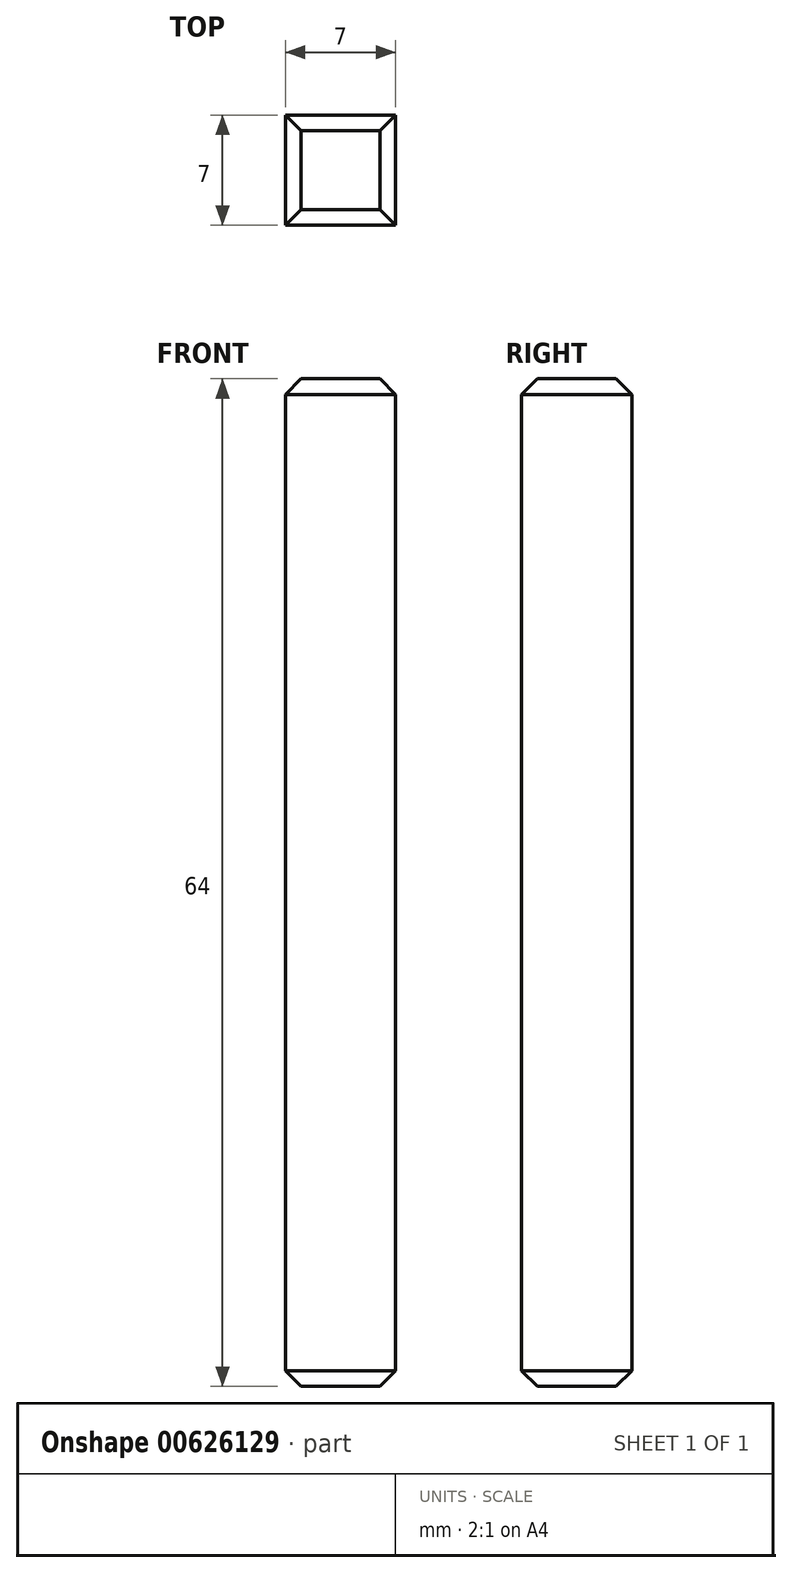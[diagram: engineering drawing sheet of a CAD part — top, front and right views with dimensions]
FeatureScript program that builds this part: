
annotation { "Feature Type Name" : "Feature", "Feature Type Description" : "" }
export const myFeature = defineFeature(function(context is Context, id is Id, definition is map)
    precondition{}
    {
        {
            var Q0;
            Q0=qCreatedBy(makeId("Front.planeOp"),FACE);
            var sketch = newSketch(context, id + "F0", { "sketchPlane" : qUnion([Q0])});
            skLineSegment(sketch, "E0.bottom", {"start": v(-3.5, 32) * mm, "end": v(3.5, 32) * mm});
            skLineSegment(sketch, "E0.top", {"start": v(-3.5, -32) * mm, "end": v(3.5, -32) * mm});
            skLineSegment(sketch, "E0.left", {"start": v(-3.5, 32) * mm, "end": v(-3.5, -32) * mm});
            skLineSegment(sketch, "E0.right", {"start": v(3.5, 32) * mm, "end": v(3.5, -32) * mm});
            skPoint(sketch, "E0.middle", {"position": v(0, 0) * mm});
            skSolve(sketch);
        }
        {
            var Q0;
            Q0=makeQuery(id+"F0.imprint","IMPRINT",FACE,{"disambiguationData":[TD([[makeQuery(id+"F0.imprint","IMPRINT",EDGE,{"derivedFrom":sQuery(id+"F0.wireOp",EDGE,"E0.bottom")}),-1.0]])]});
            extrude(context, id + "F1", {"entities" : qUnion([Q0]), "depth" : 7 * mm, "offsetDistance" : 25 * mm});
        }
        {
            var Q0;
            Q0=makeQuery(id+"F1.opExtrude","CAP_EDGE",EDGE,{"disambiguationData":[OSD([sQuery(id+"F0.wireOp",EDGE,"E0.bottom")])],"isStart":false});
            var Q1;
            Q1=makeQuery(id+"F1.opExtrude","SWEPT_EDGE",EDGE,{"disambiguationData":[OSD([sQuery(id+"F0.wireOp",EDGE,"E0.bottom"),sQuery(id+"F0.wireOp",EDGE,"E0.right")])]});
            var Q2;
            Q2=makeQuery(id+"F1.opExtrude","CAP_EDGE",EDGE,{"disambiguationData":[OSD([sQuery(id+"F0.wireOp",EDGE,"E0.bottom")])],"isStart":true});
            var Q3;
            Q3=makeQuery(id+"F1.opExtrude","SWEPT_EDGE",EDGE,{"disambiguationData":[OSD([sQuery(id+"F0.wireOp",EDGE,"E0.bottom"),sQuery(id+"F0.wireOp",EDGE,"E0.left")])]});
            var Q4;
            Q4=makeQuery(id+"F1.opExtrude","SWEPT_EDGE",EDGE,{"disambiguationData":[OSD([sQuery(id+"F0.wireOp",EDGE,"E0.top"),sQuery(id+"F0.wireOp",EDGE,"E0.right")])]});
            var Q5;
            Q5=makeQuery(id+"F1.opExtrude","CAP_EDGE",EDGE,{"disambiguationData":[OSD([sQuery(id+"F0.wireOp",EDGE,"E0.top")])],"isStart":false});
            var Q6;
            Q6=makeQuery(id+"F1.opExtrude","SWEPT_EDGE",EDGE,{"disambiguationData":[OSD([sQuery(id+"F0.wireOp",EDGE,"E0.top"),sQuery(id+"F0.wireOp",EDGE,"E0.left")])]});
            var Q7;
            Q7=makeQuery(id+"F1.opExtrude","CAP_EDGE",EDGE,{"disambiguationData":[OSD([sQuery(id+"F0.wireOp",EDGE,"E0.top")])],"isStart":true});
            chamfer(context, id + "F2", {"entities" : qUnion([Q0, Q1, Q2, Q3, Q4, Q5, Q6, Q7]), "width" : 1 * mm, "tangentPropagation" : true});
        }
    });
